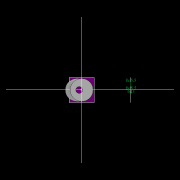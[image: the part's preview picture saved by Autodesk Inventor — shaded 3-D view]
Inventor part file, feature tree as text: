
AUTODESK INVENTOR PART (.ipt)
format: ipt  version: 2022.2 (Build 262287010, 287A)  size: 526,336 bytes
history: native  units: mm
features: other x20, extrude x19, sketch x13, pattern_circular x7, plane x5, fillet x2, move_body x2, revolve x2, draft x2, chamfer x2, loft x1
ambient origin geometry x8: Origin, YZ Plane, XZ Plane, XY Plane, X Axis, Y Axis, Z Axis, Center Point
bodies: Solid5 (feature_tree)
feature tree (75):
  other  "CrossSection1"
  sketch  "Sketch7"  dims[d90=15.767323mm]
  other  "Roller1"
  other  "Roller2"
  sketch  "Sketch22"  dims[d167=8.972256mm]
  sketch  "Sketch2"  dims[d57=4.025mm]
  sketch  "Sketch23"  dims[d173=10.814812mm]
  other  "RevRoller1"
  fillet  "Fillet1"  Radius=13.336791mm
  pattern_circular  "Circular Pattern13"  Count=360  [1 undecoded]
  move_body  "Move Body7"
  revolve  "Revolution13"  [1 undecoded]
  fillet  "Fillet3"  Radius=0.025mm
  pattern_circular  "Circular Pattern14"  [2 undecoded]
  move_body  "Move Body6"
  revolve  "Revolution14"  [1 undecoded]
  plane  "Work Plane7"
  sketch  "Sketch44"  dims[d349=17.374602mm]
  plane  "Work Plane8"
  loft  "Loft1"
  sketch  "Sketch46"  dims[d351=0.025mm]
  extrude  "Extrusion39"  Depth=5.230953mm
  plane  "Work Plane9"
  sketch  "Sketch47"  dims[d352=0.025mm d354=0.025mm d355=17.374329mm d356=17.374602mm d357=1.0mm d358=90.0deg d359=0.5mm d360=60.0mm d361=360.0deg d363=30.0deg d367=8.1mm d369=4.014775mm d370=0.025mm d371=1.0mm d372=30.0deg d373=90.0deg d374=0.5mm d375=60.0mm d376=360.0deg d378=90.0deg d379=0.1mm d380=0.025mm d381=0.025mm d382=0.025mm d383=0.025mm d384=10.461905mm d385=0.0mm d386=0.0mm d391=1.0mm d392=53.5mm d393=1.5mm d394=1.5mm d395=1.5mm d396=1.5mm d397=90.0deg d398=90.0deg d399=90.0deg d400=53.5mm d401=10.461905mm d402=0.0mm d486=0.436332mm d487=0.5mm d488=2.0mm d489=0.0mm d490=20.0mm d495=2.5mm d496=8.0mm d506=13.856406mm d507=55.5mm d508=8.0mm d509=0.05mm d510=2.5mm d511=30.0deg d512=12.0mm d513=6.0mm d514=0.2mm d515=30.0deg d516=131.0mm d517=65.5mm d518=0.2mm d519=100.0mm d520=120.0mm d521=2.0mm d522=150.0mm d530=50.0mm d531=5.5mm d532=5.5mm d533=5.5mm d534=85.75mm d535=73.5mm d536=61.25mm d537=24.5mm d538=3.0mm d539=2.4mm d540=0.0mm d541=0.0mm d542=0.0mm d543=5.5mm d544=3.0mm d545=0.0mm d546=90.0mm d547=360.0deg d549=3.0mm d550=3.0mm d551=2.4mm d552=0.0mm d553=5.230953mm d554=0.0mm d555=2.4mm d556=0.0mm d557=5.230953mm d558=0.0mm d559=5.230953mm d560=0.0mm d561=90.0mm d562=360.0deg d564=60.0mm d565=360.0deg d567=5.5mm d568=5.5mm d569=3.0mm d570=0.0mm d571=5.230953mm d572=0.0mm d573=3.0mm d574=0.0mm d575=5.230953mm d576=0.0mm d577=90.0mm d578=360.0deg d580=60.0mm d581=360.0deg d584=20.0mm d585=8.0mm d587=1.75mm d589=3.0mm d592=2.0mm d593=12.0mm d594=12.0mm d600=0.5mm d601=2.0mm d602=45.0deg d603=0.5mm d604=2.0mm d605=45.0deg d606=0.436332mm d607=0.5mm d608=0.0mm d609=20.0mm d611=360.0deg d613=0.0mm d614=0.0mm d615=20.0mm d616=3.376mm d617=0.0mm d618=90.0deg d619=0.0mm d620=90.0deg d621=2.5mm d622=7.0mm d623=0.0mm d624=0.0mm d625=50.0mm d626=5.5mm d627=3.0mm d628=5.5mm d629=43.459mm d630=0.0mm d631=52.538mm d632=0.0mm d633=4.8mm d634=0.0mm d16=0.872665mm d17=0.872665mm d49=0.872665mm d50=0.872665mm d51=0.872665mm d52=0.872665mm d236=0.5mm d237=0.872665mm d238=0.5mm d239=0.872665mm d282=1.0mm d283=1.0mm d284=1.0mm d285=0.15mm d286=0.25mm d287=0.375mm d288=14.3117mm d289=0.75mm d290=20.594885mm d291=0.0625mm d292=0.75mm d293=0.375mm d405=0.5mm d406=0.872665mm d407=0.5mm d408=0.872665mm d413=0.5mm d414=0.872665mm d415=0.5mm d416=0.872665mm d417=0.5mm d418=0.872665mm d419=0.5mm d420=0.872665mm d421=0.872665mm d431=0.5mm d432=0.872665mm d433=0.5mm d434=0.872665mm d471=0.5mm d472=0.872665mm d473=0.5mm d474=0.872665mm d497=0.5mm d498=0.872665mm d499=0.5mm d500=0.872665mm d590=0.5mm d591=0.872665mm]
  extrude  "Extrusion40"  TaperAngle=90.0deg  [1 undecoded]
  extrude  "Extrusion41"  Depth=5.230953mm
  extrude  "Extrusion42"  Depth=5.230953mm
  other  "OuterRim_Top2"
  other  "OuterRim_Bottom2"
  extrude  "Rotor_Ring"  TaperAngle=360.0deg  [1 undecoded]
  draft  "FaceDraft2"
  sketch  "Sketch30"  dims[d201=53.5mm d232=0.0mm d233=3600.0mm]
  plane  "Work Plane5"
  other  "Rotor Featurs"
  other  "RotorRim_Bottom"
  extrude  "Extrusion24"  TaperAngle=30.0deg  [1 undecoded]
  extrude  "Extrusion25"  Depth=5.230953mm
  extrude  "Extrusion26"  Depth=5.230953mm
  pattern_circular  "Circular Pattern23"  [2 undecoded]
  sketch  "Sketch41"  dims[d346=0.025mm]
  extrude  "Extrusion27"  Depth=5.230953mm
  extrude  "Extrusion28"  TaperAngle=30.0deg  [1 undecoded]
  pattern_circular  "Circular Pattern24"  Angle=90.0deg  [1 undecoded]
  extrude  "Extrusion29"  Depth=5.230953mm
  extrude  "Extrusion30"  Depth=5.230953mm
  extrude  "Extrusion31"  TaperAngle=360.0deg  [1 undecoded]
  pattern_circular  "Circular Pattern25"  Angle=90.0deg  [1 undecoded]
  sketch  "Sketch42"  dims[d347=0.1mm]
  extrude  "Extrusion32"  Depth=0.1mm
  extrude  "Extrusion33"  Depth=5.230953mm
  extrude  "Extrusion34"  Depth=5.230953mm
  extrude  "Extrusion35"  Depth=5.230953mm
  pattern_circular  "Circular Pattern26"  [2 undecoded]
  pattern_circular  "Circular Pattern27"  [2 undecoded]
  chamfer  "Chamfer1"  [1 undecoded]
  chamfer  "Chamfer2"  [1 undecoded]
  draft  "FaceDraft4"
  plane  "Work Plane6"
  sketch  "Sketch43"  dims[d348=0.1mm]
  extrude  "Extrusion37"  Depth=5.230953mm
  extrude  "Extrusion38"  Depth=5.230953mm
  other  "2D Equation Curve1"
  sketch  "Sketch40"  dims[d343=17.374329mm d344=17.374602mm d345=0.025mm]
  other  "Work Axis6"
  other  "Work Axis7"
  other  "Work Axis8"
  other  "Work Axis9"
  other  "Work Axis10"
  other  "Work Point1"
  other  "Work Point2"
  other  "Work Point3"
  other  "Work Point4"
  other  "Work Point5"
  sketch  "Sketch45"  dims[d350=17.374329mm]
  other  "Edges1"
note: 20 required parameter values undecoded (feature->parameter linkage not recoverable at this tier; creation-order binding heuristic only, values carry confidence <= 0.55)